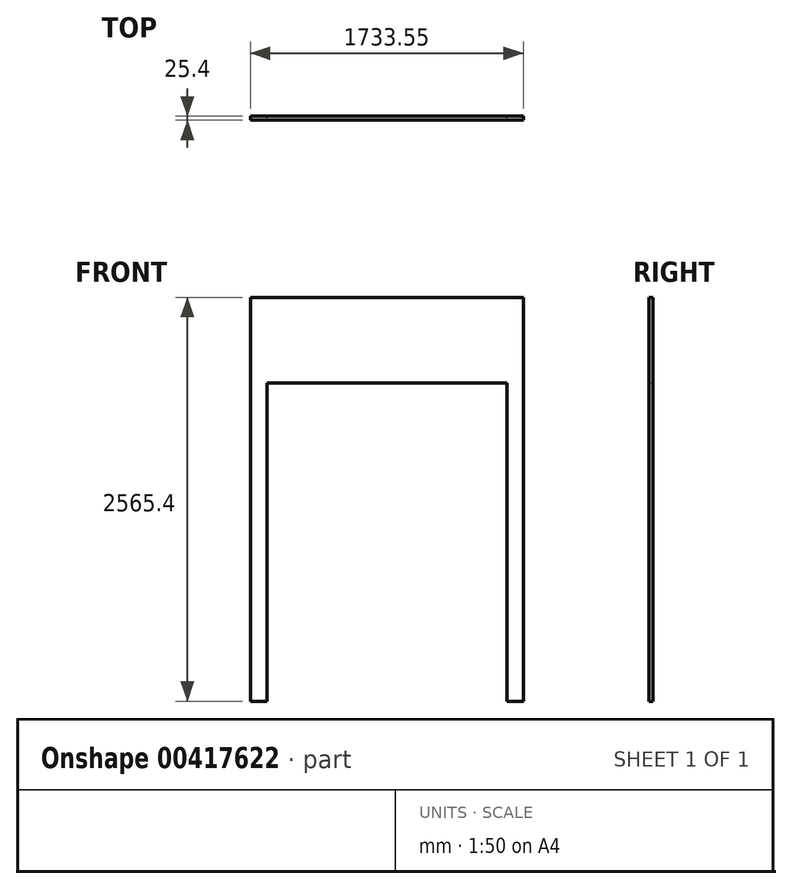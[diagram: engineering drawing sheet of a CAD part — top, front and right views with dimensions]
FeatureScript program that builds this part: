
annotation { "Feature Type Name" : "Feature", "Feature Type Description" : "" }
export const myFeature = defineFeature(function(context is Context, id is Id, definition is map)
    precondition{}
    {
        {
            var Q0;
            Q0=qCreatedBy(makeId("Front.planeOp"),FACE);
            var sketch = newSketch(context, id + "F0", { "sketchPlane" : qUnion([Q0])});
            skLineSegment(sketch, "E0.bottom", {"start": v(0, 0) * mm, "end": v(104.77, 0) * mm});
            skLineSegment(sketch, "E0.top", {"start": v(0, 2565.4) * mm, "end": v(1733.55, 2565.4) * mm});
            skLineSegment(sketch, "E0.left", {"start": v(0, 0) * mm, "end": v(0, 2565.4) * mm});
            skLineSegment(sketch, "E0.right", {"start": v(1733.55, 0) * mm, "end": v(1733.55, 2565.4) * mm});
            skLineSegment(sketch, "E1.top", {"start": v(104.77, 2022.47) * mm, "end": v(1628.77, 2022.47) * mm});
            skLineSegment(sketch, "E1.left", {"start": v(104.78, 0) * mm, "end": v(104.77, 2022.47) * mm});
            skLineSegment(sketch, "E1.right", {"start": v(1628.78, 0) * mm, "end": v(1628.77, 2022.47) * mm});
            skLineSegment(sketch, "E2.trimOffspring", {"start": v(1628.78, 0) * mm, "end": v(1733.55, 0) * mm});
            skSolve(sketch);
        }
        {
            var Q0;
            Q0 = qSketchRegion(id + "F0", true);
            extrude(context, id + "F1", {"entities" : qUnion([Q0]), "depth" : 25.4 * mm});
        }
        {
            var Q0;
            Q0=makeQuery(id+"F1.opExtrude","SWEPT_BODY",BODY,{"disambiguationData":[OSD([sQuery(id+"F0.wireOp",EDGE,"E0.bottom"),sQuery(id+"F0.wireOp",EDGE,"E0.top"),sQuery(id+"F0.wireOp",EDGE,"E0.left"),sQuery(id+"F0.wireOp",EDGE,"E0.right"),sQuery(id+"F0.wireOp",EDGE,"E1.top"),sQuery(id+"F0.wireOp",EDGE,"E1.left"),sQuery(id+"F0.wireOp",EDGE,"E1.right"),sQuery(id+"F0.wireOp",EDGE,"E2.trimOffspring")])]});
            transform(context, id + "F2", {"entities" : qUnion([Q0]), "transformType" : TransformType.TRANSLATION_3D, "dx" : 0 * mm, "dy" : 0 * mm, "dz" : 0 * mm, "makeCopy" : true});
        }
    });
